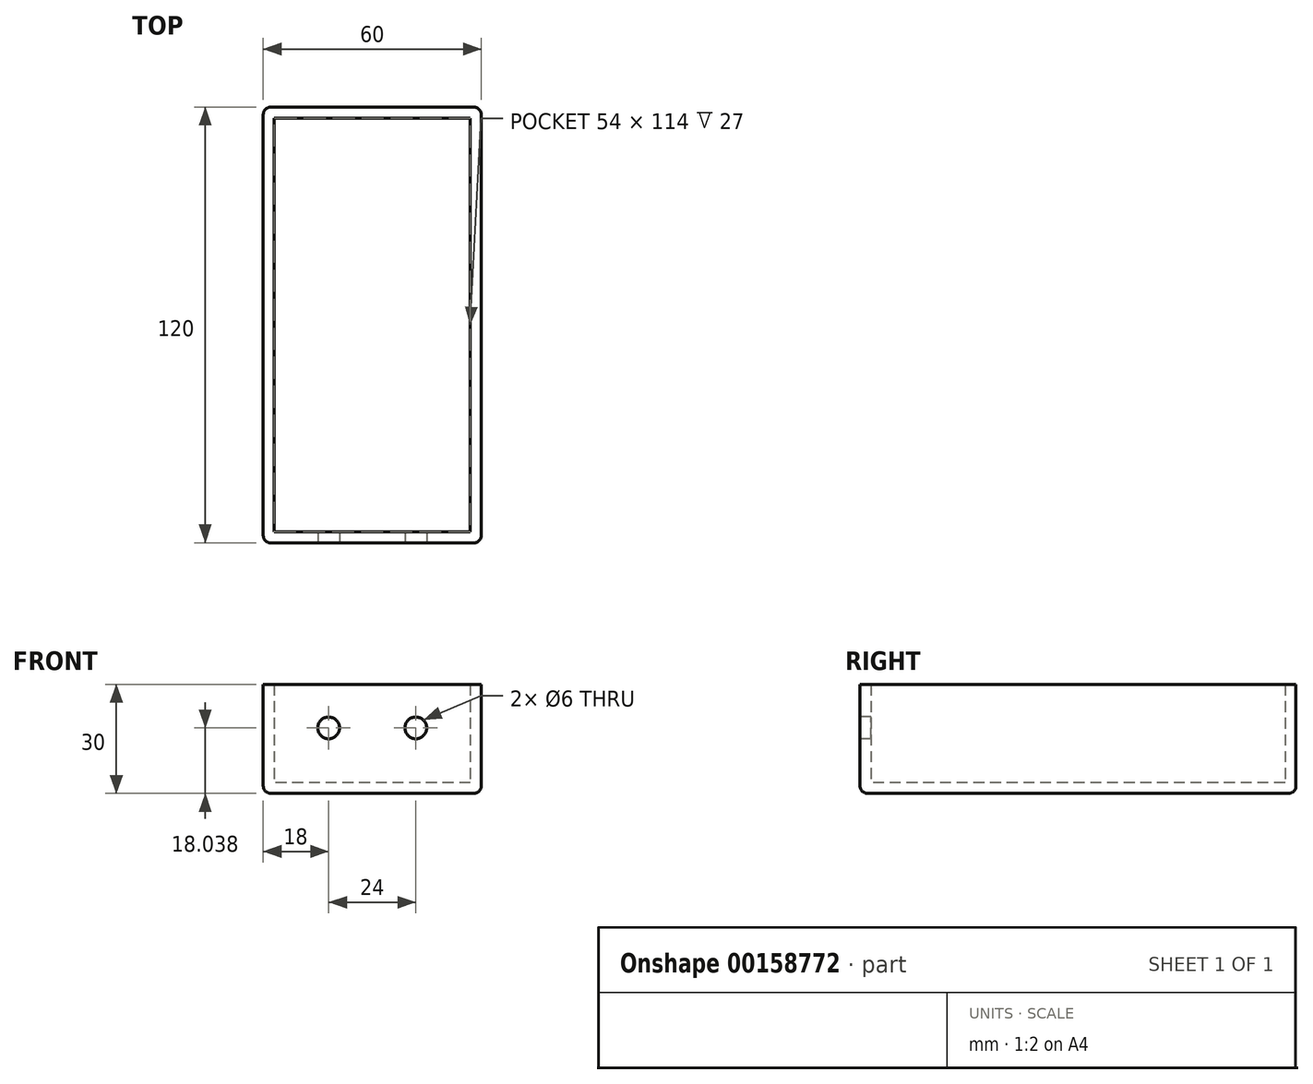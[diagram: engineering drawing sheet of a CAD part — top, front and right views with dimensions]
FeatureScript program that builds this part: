
annotation { "Feature Type Name" : "Feature", "Feature Type Description" : "" }
export const myFeature = defineFeature(function(context is Context, id is Id, definition is map)
    precondition{}
    {
        {
            var Q0;
            Q0=qCreatedBy(makeId("Top.planeOp"),FACE);
            var sketch = newSketch(context, id + "F0", { "sketchPlane" : qUnion([Q0])});
            skLineSegment(sketch, "E0.bottom", {"start": v(30, 60) * mm, "end": v(-30, 60) * mm});
            skLineSegment(sketch, "E0.top", {"start": v(30, -60) * mm, "end": v(-30, -60) * mm});
            skLineSegment(sketch, "E0.left", {"start": v(30, 60) * mm, "end": v(30, -60) * mm});
            skLineSegment(sketch, "E0.right", {"start": v(-30, 60) * mm, "end": v(-30, -60) * mm});
            skPoint(sketch, "E0.middle", {"position": v(0, 0) * mm});
            skSolve(sketch);
        }
        {
            var Q0;
            Q0=makeQuery(id+"F0.imprint","IMPRINT",FACE,{"disambiguationData":[TD([[makeQuery(id+"F0.imprint","IMPRINT",EDGE,{"derivedFrom":sQuery(id+"F0.wireOp",EDGE,"E0.bottom")}),1.0]])]});
            extrude(context, id + "F1", {"entities" : qUnion([Q0]), "depth" : 30 * mm});
        }
        {
            var Q0;
            Q0=makeQuery(id+"F1.opExtrude","CAP_FACE",FACE,{"disambiguationData":[OSD([sQuery(id+"F0.wireOp",EDGE,"E0.bottom"),sQuery(id+"F0.wireOp",EDGE,"E0.top"),sQuery(id+"F0.wireOp",EDGE,"E0.left"),sQuery(id+"F0.wireOp",EDGE,"E0.right")])],"isStart":false});
            shell(context, id + "F2", {"entities" : qUnion([Q0]), "thickness" : 3 * mm});
        }
        {
            var Q0;
            Q0=makeQuery(id+"F1.opExtrude","SWEPT_EDGE",EDGE,{"disambiguationData":[OSD([sQuery(id+"F0.wireOp",EDGE,"E0.top"),sQuery(id+"F0.wireOp",EDGE,"E0.left")])]});
            var Q1;
            Q1=makeQuery(id+"F1.opExtrude","SWEPT_EDGE",EDGE,{"disambiguationData":[OSD([sQuery(id+"F0.wireOp",EDGE,"E0.bottom"),sQuery(id+"F0.wireOp",EDGE,"E0.left")])]});
            var Q2;
            Q2=makeQuery(id+"F1.opExtrude","SWEPT_EDGE",EDGE,{"disambiguationData":[OSD([sQuery(id+"F0.wireOp",EDGE,"E0.bottom"),sQuery(id+"F0.wireOp",EDGE,"E0.right")])]});
            var Q3;
            Q3=makeQuery(id+"F1.opExtrude","SWEPT_EDGE",EDGE,{"disambiguationData":[OSD([sQuery(id+"F0.wireOp",EDGE,"E0.top"),sQuery(id+"F0.wireOp",EDGE,"E0.right")])]});
            fillet(context, id + "F3", {"entities" : qUnion([Q0, Q1, Q2, Q3]), "radius" : 2 * mm, "tangentPropagation" : true, "allowEdgeOverflow" : false});
        }
        {
            var Q0;
            Q0=makeQuery(id+"F1.opExtrude","SWEPT_FACE",FACE,{"disambiguationData":[OSD([sQuery(id+"F0.wireOp",EDGE,"E0.top")])]});
            var sketch = newSketch(context, id + "F4", { "sketchPlane" : qUnion([Q0])});
            skCircle(sketch, "E1", {"center": v(-12, 18.04) * mm, "radius": 3 * mm});
            skCircle(sketch, "E2.MirrorC", {"center": v(12, 18.04) * mm, "radius": 3 * mm});
            skSolve(sketch);
        }
        {
            var Q0;
            Q0=sQuery(id+"F4.wireOp",VERTEX,"E1.center");
            var Q1;
            Q1=sQuery(id+"F4.wireOp",VERTEX,"E2.MirrorC.center");
            var Q2;
            Q2=makeQuery(id+"F1.opExtrude","SWEPT_BODY",BODY,{"disambiguationData":[OSD([sQuery(id+"F0.wireOp",EDGE,"E0.bottom"),sQuery(id+"F0.wireOp",EDGE,"E0.top"),sQuery(id+"F0.wireOp",EDGE,"E0.left"),sQuery(id+"F0.wireOp",EDGE,"E0.right")])]});
            hole(context, id + "F5", {"style" : HoleStyle.SIMPLE, "endStyle" : HoleEndStyle.BLIND, "holeDiameter" : 6 * mm, "holeDepth" : 12 * mm, "locations" : qUnion([Q0, Q1]), "scope" : qUnion([Q2])});
        }
        {
            var Q0;
            Q0=makeQuery(id+"F1.opExtrude","CAP_FACE",FACE,{"disambiguationData":[OSD([sQuery(id+"F0.wireOp",EDGE,"E0.bottom"),sQuery(id+"F0.wireOp",EDGE,"E0.top"),sQuery(id+"F0.wireOp",EDGE,"E0.left"),sQuery(id+"F0.wireOp",EDGE,"E0.right")])],"isStart":true});
            fillet(context, id + "F6", {"entities" : qUnion([Q0]), "radius" : 2 * mm, "tangentPropagation" : true, "allowEdgeOverflow" : false});
        }
    });
